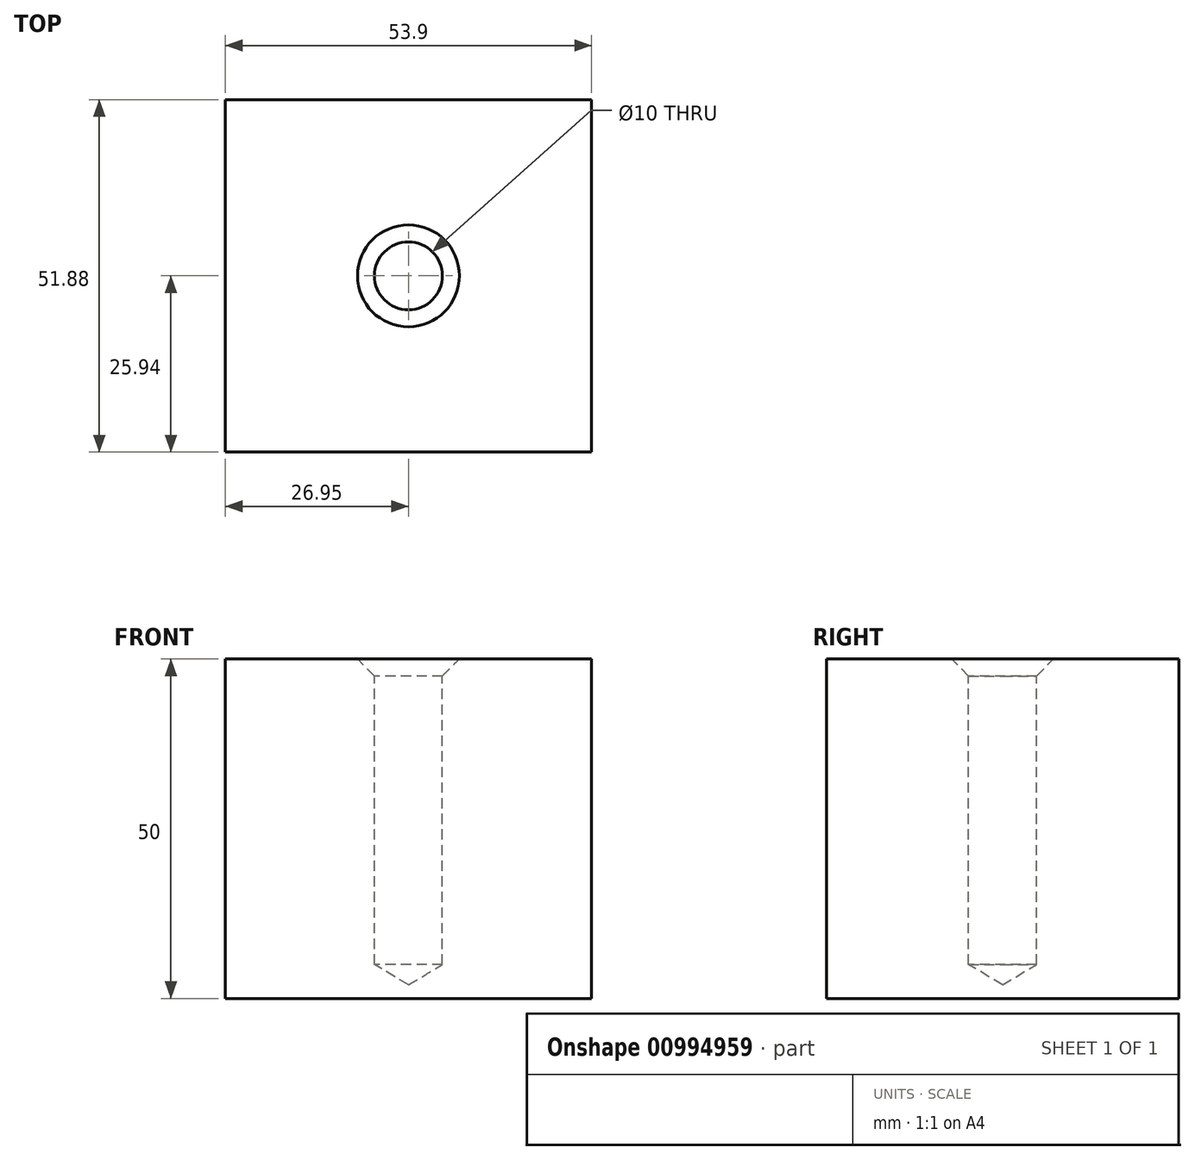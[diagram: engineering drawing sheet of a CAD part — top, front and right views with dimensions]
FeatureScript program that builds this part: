
annotation { "Feature Type Name" : "Feature", "Feature Type Description" : "" }
export const myFeature = defineFeature(function(context is Context, id is Id, definition is map)
    precondition{}
    {
        {
            var Q0;
            Q0=qCreatedBy(makeId("Top.planeOp"),FACE);
            var sketch = newSketch(context, id + "F0", { "sketchPlane" : qUnion([Q0])});
            skLineSegment(sketch, "E0.bottom", {"start": v(26.95, -25.94) * mm, "end": v(-26.95, -25.94) * mm});
            skLineSegment(sketch, "E0.top", {"start": v(26.95, 25.94) * mm, "end": v(-26.95, 25.94) * mm});
            skLineSegment(sketch, "E0.left", {"start": v(26.95, -25.94) * mm, "end": v(26.95, 25.94) * mm});
            skLineSegment(sketch, "E0.right", {"start": v(-26.95, -25.94) * mm, "end": v(-26.95, 25.94) * mm});
            skPoint(sketch, "E0.middle", {"position": v(0, 0) * mm});
            skSolve(sketch);
        }
        {
            var Q0;
            Q0 = qSketchRegion(id + "F0", true);
            extrude(context, id + "F1", {"entities" : qUnion([Q0]), "endBound" : BoundingType.SYMMETRIC, "depth" : 50 * mm, "offsetDistance" : 25 * mm});
        }
        {
            var Q0;
            Q0=makeQuery(id+"F1.opExtrude","CAP_FACE",FACE,{"disambiguationData":[OSD([sQuery(id+"F0.wireOp",EDGE,"E0.bottom"),sQuery(id+"F0.wireOp",EDGE,"E0.top"),sQuery(id+"F0.wireOp",EDGE,"E0.left"),sQuery(id+"F0.wireOp",EDGE,"E0.right")])],"isStart":false});
            var sketch = newSketch(context, id + "F2", { "sketchPlane" : qUnion([Q0])});
            skPoint(sketch, "E1", {"position": v(0, 0) * mm});
            skSolve(sketch);
        }
        {
            var Q0;
            Q0=sQuery(id+"F2.wireOp",VERTEX,"E1");
            var Q1;
            Q1=makeQuery(id+"F1.opExtrude","SWEPT_BODY",BODY,{"disambiguationData":[OSD([sQuery(id+"F0.wireOp",EDGE,"E0.bottom"),sQuery(id+"F0.wireOp",EDGE,"E0.top"),sQuery(id+"F0.wireOp",EDGE,"E0.left"),sQuery(id+"F0.wireOp",EDGE,"E0.right")])]});
            hole(context, id + "F3", {"style" : HoleStyle.C_SINK, "endStyle" : HoleEndStyle.BLIND, "holeDiameter" : 10 * mm, "cSinkDiameter" : 15 * mm, "cSinkAngle" : 90 * degree, "majorDiameter" : 5 * mm, "holeDepth" : 45 * mm, "isTappedThrough" : true, "tappedDepth" : 12 * mm, "tapClearance" : 3, "startFromSketch" : true, "locations" : qUnion([Q0]), "scope" : qUnion([Q1])});
        }
    });
